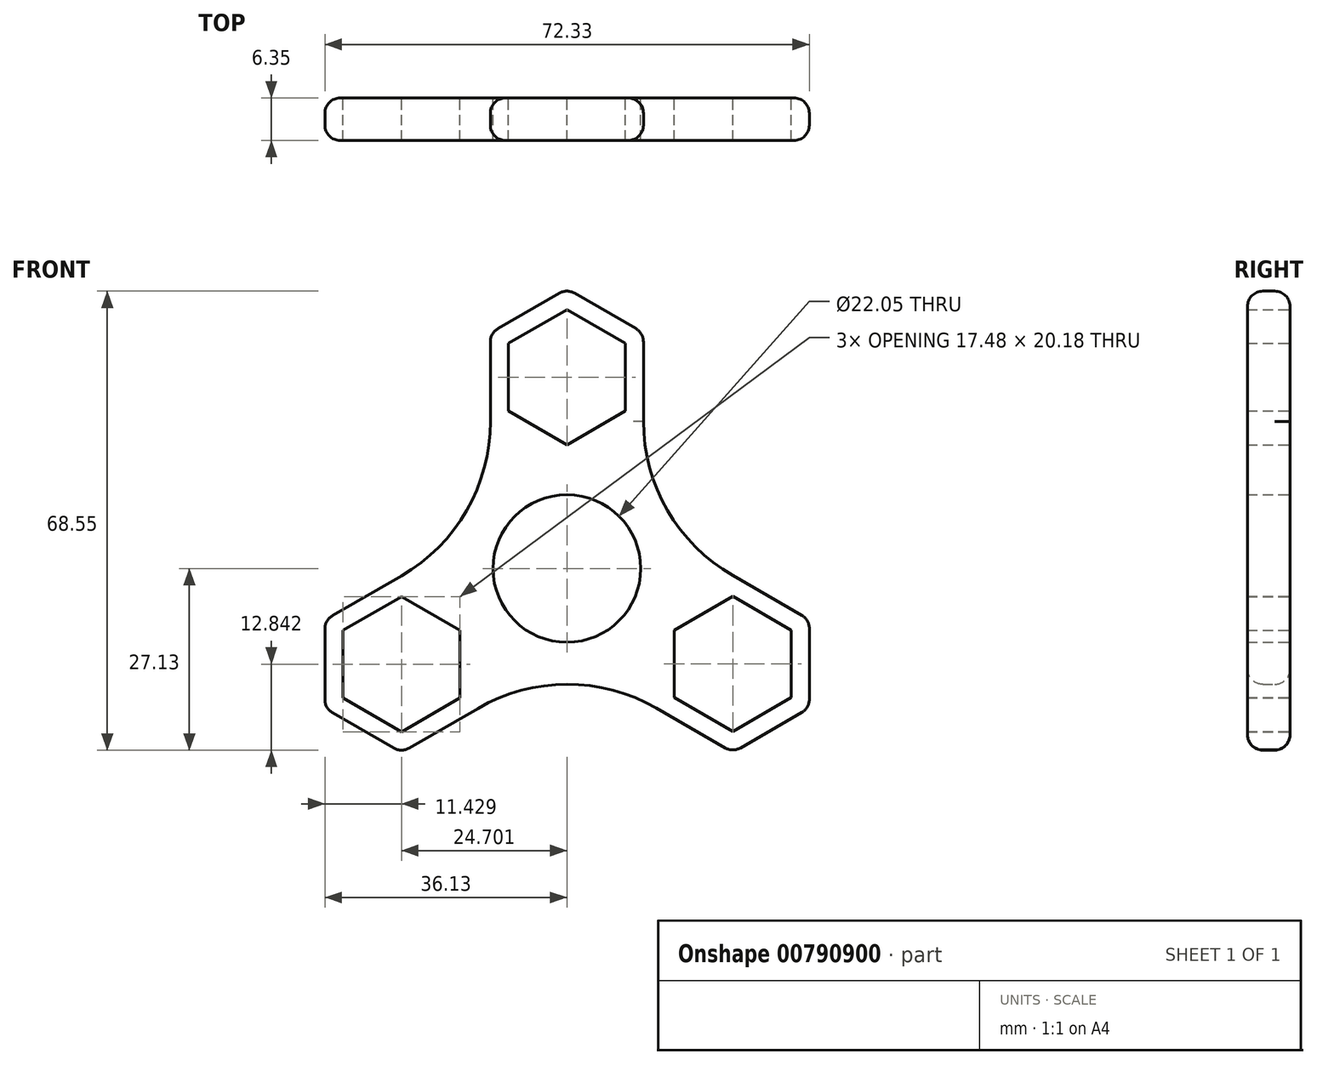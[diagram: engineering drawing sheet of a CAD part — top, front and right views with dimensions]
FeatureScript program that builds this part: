
annotation { "Feature Type Name" : "Feature", "Feature Type Description" : "" }
export const myFeature = defineFeature(function(context is Context, id is Id, definition is map)
    precondition{}
    {
        {
            var Q0;
            Q0=qCreatedBy(makeId("Front.planeOp"),FACE);
            var sketch = newSketch(context, id + "F0", { "sketchPlane" : qUnion([Q0])});
            skCircle(sketch, "E0", {"center": v(0, 0) * mm, "radius": 11.02 * mm});
            skCircle(sketch, "E1", {"center": v(0, 0) * mm, "radius": 14.29 * mm});
            skCircle(sketch, "E2.cCircle", {"center": v(0, 28.58) * mm, "radius": 8.74 * mm, "construction": true});
            skLineSegment(sketch, "E2.0", {"start": v(-8.74, 23.53) * mm, "end": v(-8.74, 33.62) * mm});
            skLineSegment(sketch, "E2.1", {"start": v(-8.74, 33.62) * mm, "end": v(0, 38.66) * mm});
            skLineSegment(sketch, "E2.2", {"start": v(0, 38.66) * mm, "end": v(8.74, 33.62) * mm});
            skLineSegment(sketch, "E2.3", {"start": v(8.74, 33.62) * mm, "end": v(8.74, 23.53) * mm});
            skLineSegment(sketch, "E2.4", {"start": v(8.74, 23.53) * mm, "end": v(0, 18.49) * mm});
            skLineSegment(sketch, "E2.5", {"start": v(0, 18.49) * mm, "end": v(-8.74, 23.53) * mm});
            skPoint(sketch, "E2.0.midPoint", {"position": v(-8.74, 28.58) * mm});
            skCircle(sketch, "E3.cCircle", {"center": v(0, 28.58) * mm, "radius": 11.43 * mm, "construction": true});
            skLineSegment(sketch, "E3.0", {"start": v(-11.43, 21.98) * mm, "end": v(-11.43, 35.17) * mm});
            skLineSegment(sketch, "E3.1", {"start": v(-11.43, 35.17) * mm, "end": v(0, 41.77) * mm});
            skLineSegment(sketch, "E3.2", {"start": v(0, 41.77) * mm, "end": v(11.43, 35.17) * mm});
            skLineSegment(sketch, "E3.3", {"start": v(11.43, 35.17) * mm, "end": v(11.43, 21.98) * mm});
            skLineSegment(sketch, "E3.4", {"start": v(11.43, 21.98) * mm, "end": v(0, 15.38) * mm});
            skLineSegment(sketch, "E3.5", {"start": v(0, 15.38) * mm, "end": v(-11.43, 21.98) * mm});
            skPoint(sketch, "E3.0.midPoint", {"position": v(-11.43, 28.58) * mm});
            skPoint(sketch, "E4.1.0", {"position": v(-18.99, -24.19) * mm});
            skCircle(sketch, "E4.1.1", {"center": v(-24.7, -14.29) * mm, "radius": 8.74 * mm, "construction": true});
            skLineSegment(sketch, "E4.1.2", {"start": v(-33.44, -19.33) * mm, "end": v(-33.44, -9.24) * mm});
            skLineSegment(sketch, "E4.1.3", {"start": v(-13.27, -7.69) * mm, "end": v(-13.27, -20.89) * mm});
            skLineSegment(sketch, "E4.1.4", {"start": v(-24.7, -1.09) * mm, "end": v(-13.27, -7.69) * mm});
            skLineSegment(sketch, "E4.1.5", {"start": v(-36.13, -7.69) * mm, "end": v(-24.7, -1.09) * mm});
            skLineSegment(sketch, "E4.1.6", {"start": v(-24.7, -24.38) * mm, "end": v(-33.44, -19.33) * mm});
            skLineSegment(sketch, "E4.1.7", {"start": v(-33.44, -9.24) * mm, "end": v(-24.7, -4.2) * mm});
            skLineSegment(sketch, "E4.1.8", {"start": v(-15.96, -9.24) * mm, "end": v(-15.96, -19.33) * mm});
            skCircle(sketch, "E4.1.9", {"center": v(-24.7, -14.29) * mm, "radius": 11.43 * mm, "construction": true});
            skLineSegment(sketch, "E4.1.10", {"start": v(-13.27, -20.89) * mm, "end": v(-24.7, -27.49) * mm});
            skLineSegment(sketch, "E4.1.11", {"start": v(-24.7, -27.49) * mm, "end": v(-36.13, -20.89) * mm});
            skLineSegment(sketch, "E4.1.12", {"start": v(-36.13, -20.89) * mm, "end": v(-36.13, -7.69) * mm});
            skPoint(sketch, "E4.1.13", {"position": v(-20.33, -21.85) * mm});
            skLineSegment(sketch, "E4.1.14", {"start": v(-15.96, -19.33) * mm, "end": v(-24.7, -24.38) * mm});
            skLineSegment(sketch, "E4.1.15", {"start": v(-24.7, -4.2) * mm, "end": v(-15.96, -9.24) * mm});
            skPoint(sketch, "E4.2.0", {"position": v(30.48, -4.35) * mm});
            skCircle(sketch, "E4.2.1", {"center": v(24.77, -14.25) * mm, "radius": 8.74 * mm, "construction": true});
            skLineSegment(sketch, "E4.2.2", {"start": v(33.5, -19.3) * mm, "end": v(24.77, -24.34) * mm});
            skLineSegment(sketch, "E4.2.3", {"start": v(13.34, -7.65) * mm, "end": v(24.77, -1.05) * mm});
            skLineSegment(sketch, "E4.2.4", {"start": v(13.34, -20.85) * mm, "end": v(13.34, -7.65) * mm});
            skLineSegment(sketch, "E4.2.5", {"start": v(24.77, -27.45) * mm, "end": v(13.34, -20.85) * mm});
            skLineSegment(sketch, "E4.2.6", {"start": v(33.5, -9.2) * mm, "end": v(33.5, -19.3) * mm});
            skLineSegment(sketch, "E4.2.7", {"start": v(24.77, -24.34) * mm, "end": v(16.03, -19.3) * mm});
            skLineSegment(sketch, "E4.2.8", {"start": v(16.03, -9.2) * mm, "end": v(24.77, -4.16) * mm});
            skCircle(sketch, "E4.2.9", {"center": v(24.77, -14.25) * mm, "radius": 11.43 * mm, "construction": true});
            skLineSegment(sketch, "E4.2.10", {"start": v(24.77, -1.05) * mm, "end": v(36.2, -7.65) * mm});
            skLineSegment(sketch, "E4.2.11", {"start": v(36.2, -7.65) * mm, "end": v(36.2, -20.85) * mm});
            skLineSegment(sketch, "E4.2.12", {"start": v(36.2, -20.85) * mm, "end": v(24.77, -27.45) * mm});
            skPoint(sketch, "E4.2.13", {"position": v(29.14, -6.68) * mm});
            skLineSegment(sketch, "E4.2.14", {"start": v(24.77, -4.16) * mm, "end": v(33.5, -9.2) * mm});
            skLineSegment(sketch, "E4.2.15", {"start": v(16.03, -19.3) * mm, "end": v(16.03, -9.2) * mm});
            skPoint(sketch, "E4.center", {"position": v(0.02, 0.01) * mm});
            skArc(sketch, "E5", {"start": v(-24.7, -1.09) * mm, "mid": v(-14.97, 8.66) * mm, "end": v(-11.43, 21.98) * mm});
            skArc(sketch, "E6", {"start": v(11.43, 21.98) * mm, "mid": v(15.02, 8.68) * mm, "end": v(24.77, -1.05) * mm});
            skArc(sketch, "E7", {"start": v(13.34, -20.85) * mm, "mid": v(0.03, -17.3) * mm, "end": v(-13.27, -20.89) * mm});
            skSolve(sketch);
        }
        {
            var Q0;
            Q0 = qSketchRegion(id + "F0", true);
            var Q1;
            Q1=makeQuery(id+"F0.imprint","IMPRINT",FACE,{"disambiguationData":[TD([[makeQuery(id+"F0.imprint","IMPRINT",EDGE,{"derivedFrom":sQuery(id+"F0.wireOp",EDGE,"E0")}),-1.0]])]});
            extrude(context, id + "F1", {"entities" : qUnion([Q0, Q1]), "depth" : 6.35 * mm, "offsetDistance" : 25.4 * mm});
        }
        {
            var Q0;
            Q0=makeQuery(id+"F1.opExtrude","CAP_EDGE",EDGE,{"disambiguationData":[OSD([sQuery(id+"F0.wireOp",EDGE,"E7")])],"isStart":false});
            var Q1;
            Q1=makeQuery(id+"F1.opExtrude","CAP_EDGE",EDGE,{"disambiguationData":[OSD([sQuery(id+"F0.wireOp",EDGE,"E4.2.12")])],"isStart":false});
            var Q2;
            Q2=makeQuery(id+"F1.opExtrude","CAP_EDGE",EDGE,{"disambiguationData":[OSD([sQuery(id+"F0.wireOp",EDGE,"E4.2.11")])],"isStart":false});
            var Q3;
            Q3=makeQuery(id+"F1.opExtrude","CAP_EDGE",EDGE,{"disambiguationData":[OSD([sQuery(id+"F0.wireOp",EDGE,"E6")])],"isStart":false});
            var Q4;
            Q4=makeQuery(id+"F1.opExtrude","CAP_EDGE",EDGE,{"disambiguationData":[OSD([sQuery(id+"F0.wireOp",EDGE,"E3.3")])],"isStart":false});
            var Q5;
            Q5=makeQuery(id+"F1.opExtrude","CAP_EDGE",EDGE,{"disambiguationData":[OSD([sQuery(id+"F0.wireOp",EDGE,"E3.2")])],"isStart":false});
            var Q6;
            Q6=makeQuery(id+"F1.opExtrude","CAP_EDGE",EDGE,{"disambiguationData":[OSD([sQuery(id+"F0.wireOp",EDGE,"E3.1")])],"isStart":false});
            var Q7;
            Q7=makeQuery(id+"F1.opExtrude","CAP_EDGE",EDGE,{"disambiguationData":[OSD([sQuery(id+"F0.wireOp",EDGE,"E3.0")])],"isStart":false});
            var Q8;
            Q8=makeQuery(id+"F1.opExtrude","CAP_EDGE",EDGE,{"disambiguationData":[OSD([sQuery(id+"F0.wireOp",EDGE,"E5")])],"isStart":false});
            var Q9;
            Q9=makeQuery(id+"F1.opExtrude","CAP_EDGE",EDGE,{"disambiguationData":[OSD([sQuery(id+"F0.wireOp",EDGE,"E4.1.12")])],"isStart":false});
            var Q10;
            Q10=makeQuery(id+"F1.opExtrude","CAP_EDGE",EDGE,{"disambiguationData":[OSD([sQuery(id+"F0.wireOp",EDGE,"E4.1.11")])],"isStart":false});
            var Q11;
            Q11=makeQuery(id+"F1.opExtrude","CAP_EDGE",EDGE,{"disambiguationData":[OSD([sQuery(id+"F0.wireOp",EDGE,"E4.1.10")])],"isStart":false});
            var Q12;
            Q12=makeQuery(id+"F1.opExtrude","CAP_EDGE",EDGE,{"disambiguationData":[OSD([sQuery(id+"F0.wireOp",EDGE,"E4.1.12")])],"isStart":true});
            var Q13;
            Q13=makeQuery(id+"F1.opExtrude","CAP_EDGE",EDGE,{"disambiguationData":[OSD([sQuery(id+"F0.wireOp",EDGE,"E4.1.5")])],"isStart":true});
            var Q14;
            Q14=makeQuery(id+"F1.opExtrude","CAP_EDGE",EDGE,{"disambiguationData":[OSD([sQuery(id+"F0.wireOp",EDGE,"E3.0")])],"isStart":true});
            var Q15;
            Q15=makeQuery(id+"F1.opExtrude","CAP_EDGE",EDGE,{"disambiguationData":[OSD([sQuery(id+"F0.wireOp",EDGE,"E3.1")])],"isStart":true});
            var Q16;
            Q16=makeQuery(id+"F1.opExtrude","CAP_EDGE",EDGE,{"disambiguationData":[OSD([sQuery(id+"F0.wireOp",EDGE,"E3.2")])],"isStart":true});
            var Q17;
            Q17=makeQuery(id+"F1.opExtrude","CAP_EDGE",EDGE,{"disambiguationData":[OSD([sQuery(id+"F0.wireOp",EDGE,"E4.2.10")])],"isStart":false});
            var Q18;
            Q18=makeQuery(id+"F1.opExtrude","CAP_EDGE",EDGE,{"disambiguationData":[OSD([sQuery(id+"F0.wireOp",EDGE,"E3.3")])],"isStart":true});
            var Q19;
            Q19=makeQuery(id+"F1.opExtrude","CAP_EDGE",EDGE,{"disambiguationData":[OSD([sQuery(id+"F0.wireOp",EDGE,"E6")])],"isStart":true});
            var Q20;
            Q20=makeQuery(id+"F1.opExtrude","CAP_EDGE",EDGE,{"disambiguationData":[OSD([sQuery(id+"F0.wireOp",EDGE,"E7")])],"isStart":true});
            var Q21;
            Q21=makeQuery(id+"F1.opExtrude","CAP_EDGE",EDGE,{"disambiguationData":[OSD([sQuery(id+"F0.wireOp",EDGE,"E4.2.12")])],"isStart":true});
            var Q22;
            Q22=makeQuery(id+"F1.opExtrude","CAP_EDGE",EDGE,{"disambiguationData":[OSD([sQuery(id+"F0.wireOp",EDGE,"E4.2.5")])],"isStart":true});
            var Q23;
            Q23=makeQuery(id+"F1.opExtrude","CAP_EDGE",EDGE,{"disambiguationData":[OSD([sQuery(id+"F0.wireOp",EDGE,"E4.1.5")])],"isStart":false});
            var Q24;
            Q24=makeQuery(id+"F1.opExtrude","CAP_EDGE",EDGE,{"disambiguationData":[OSD([sQuery(id+"F0.wireOp",EDGE,"E4.2.5")])],"isStart":false});
            var Q25;
            Q25=makeQuery(id+"F1.opExtrude","CAP_EDGE",EDGE,{"disambiguationData":[OSD([sQuery(id+"F0.wireOp",EDGE,"E4.1.11")])],"isStart":true});
            var Q26;
            Q26=makeQuery(id+"F1.opExtrude","CAP_EDGE",EDGE,{"disambiguationData":[OSD([sQuery(id+"F0.wireOp",EDGE,"E4.2.11")])],"isStart":true});
            var Q27;
            Q27=makeQuery(id+"F1.opExtrude","CAP_EDGE",EDGE,{"disambiguationData":[OSD([sQuery(id+"F0.wireOp",EDGE,"E5")])],"isStart":true});
            var Q28;
            Q28=makeQuery(id+"F1.opExtrude","CAP_EDGE",EDGE,{"disambiguationData":[OSD([sQuery(id+"F0.wireOp",EDGE,"E4.2.10")])],"isStart":true});
            var Q29;
            Q29=makeQuery(id+"F1.opExtrude","CAP_EDGE",EDGE,{"disambiguationData":[OSD([sQuery(id+"F0.wireOp",EDGE,"E4.1.10")])],"isStart":true});
            var Q30;
            Q30=makeQuery(id+"F1.opExtrude","SWEPT_EDGE",EDGE,{"disambiguationData":[OSD([sQuery(id+"F0.wireOp",EDGE,"E3.1"),sQuery(id+"F0.wireOp",EDGE,"E3.2")])]});
            var Q31;
            Q31=makeQuery(id+"F1.opExtrude","SWEPT_EDGE",EDGE,{"disambiguationData":[OSD([sQuery(id+"F0.wireOp",EDGE,"E3.0"),sQuery(id+"F0.wireOp",EDGE,"E3.1")])]});
            var Q32;
            Q32=makeQuery(id+"F1.opExtrude","SWEPT_EDGE",EDGE,{"disambiguationData":[OSD([sQuery(id+"F0.wireOp",EDGE,"E3.0"),sQuery(id+"F0.wireOp",EDGE,"E3.5"),sQuery(id+"F0.wireOp",EDGE,"E5")])]});
            var Q33;
            Q33=makeQuery(id+"F1.opExtrude","SWEPT_EDGE",EDGE,{"disambiguationData":[OSD([sQuery(id+"F0.wireOp",EDGE,"E4.1.5"),sQuery(id+"F0.wireOp",EDGE,"E4.1.12")])]});
            var Q34;
            Q34=makeQuery(id+"F1.opExtrude","SWEPT_EDGE",EDGE,{"disambiguationData":[OSD([sQuery(id+"F0.wireOp",EDGE,"E4.1.11"),sQuery(id+"F0.wireOp",EDGE,"E4.1.12")])]});
            var Q35;
            Q35=makeQuery(id+"F1.opExtrude","SWEPT_EDGE",EDGE,{"disambiguationData":[OSD([sQuery(id+"F0.wireOp",EDGE,"E4.1.10"),sQuery(id+"F0.wireOp",EDGE,"E4.1.11")])]});
            var Q36;
            Q36=makeQuery(id+"F1.opExtrude","SWEPT_EDGE",EDGE,{"disambiguationData":[OSD([sQuery(id+"F0.wireOp",EDGE,"E4.2.5"),sQuery(id+"F0.wireOp",EDGE,"E4.2.12")])]});
            var Q37;
            Q37=makeQuery(id+"F1.opExtrude","SWEPT_EDGE",EDGE,{"disambiguationData":[OSD([sQuery(id+"F0.wireOp",EDGE,"E4.2.11"),sQuery(id+"F0.wireOp",EDGE,"E4.2.12")])]});
            var Q38;
            Q38=makeQuery(id+"F1.opExtrude","SWEPT_EDGE",EDGE,{"disambiguationData":[OSD([sQuery(id+"F0.wireOp",EDGE,"E4.2.10"),sQuery(id+"F0.wireOp",EDGE,"E4.2.11")])]});
            var Q39;
            Q39=makeQuery(id+"F1.opExtrude","SWEPT_EDGE",EDGE,{"disambiguationData":[OSD([sQuery(id+"F0.wireOp",EDGE,"E3.2"),sQuery(id+"F0.wireOp",EDGE,"E3.3")])]});
            fillet(context, id + "F2", {"entities" : qUnion([Q0, Q1, Q2, Q3, Q4, Q5, Q6, Q7, Q8, Q9, Q10, Q11, Q12, Q13, Q14, Q15, Q16, Q17, Q18, Q19, Q20, Q21, Q22, Q23, Q24, Q25, Q26, Q27, Q28, Q29, Q30, Q31, Q32, Q33, Q34, Q35, Q36, Q37, Q38, Q39]), "radius" : 2.3 * mm, "tangentPropagation" : true, "allowEdgeOverflow" : false});
        }
    });
